# Revit family: Juxta_Lounge_Chair_Low_Back_With_Arms_Models_45320_45330_45340_45341_45350_45351
name_source: partatom
category: Furniture
units: mm (PartAtom-declared; Revit-internal decimal feet)

## family parameters
Always vertical = Yes
Cut with Voids When Loaded = No
OmniClass Number = 23.40.70.14.64.11
OmniClass Title = Office Furniture
Room Calculation Point = No
Shared = No
Work Plane-Based = No

## types (6) — shared parameters
Assembly Code = E2020200
Catalog = JUXTA
Manufacturer = Keilhauer, Corp.
Product Documentation Link = http://www.keilhauer.com
URL = http://www.keilhauer.com
zero-valued in all types: Default Elevation

## per-type parameters (varying)
| type | Cushion | Five Star | Four Legs | Four Star | Model | Sled Base | Tablet |
| Low Back Chair with Arms 4 Leg Base | Yes | No | Yes | No | 45320 | No | No |
| Low Back Chair with Arms Sled Base | Yes | No | No | No | 45330 | Yes | No |
| Low Back Chair with Arms 4 Star Base | Yes | No | No | Yes | 45340 | No | No |
| Low Back Chair with Arms 4 Star Base with Tablet | No | No | No | Yes | 45341 | No | Yes |
| Low Back Chair with Arms 5 Star Base | Yes | Yes | No | No | 45350 | No | No |
| Low Back Chair with Arms 5 Star Base with Tablet | No | Yes | No | No | 45351 | No | Yes |

note: column(s) folded — value = type name in every type: Description

## geometry (parser evidence)
native form markers: Sweep x7
no freeform markers — native parametric forms only
